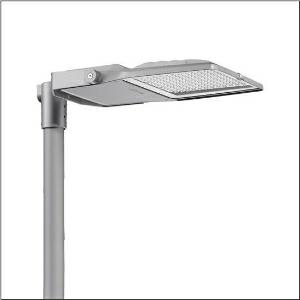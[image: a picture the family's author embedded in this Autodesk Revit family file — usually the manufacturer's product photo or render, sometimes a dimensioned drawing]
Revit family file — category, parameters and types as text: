
# Revit family: floodlight_fl_21_iq_midi___pl33t_5xa7782e4f3a_344b
name_source: partatom
category: Lighting Fixtures
units: mm (PartAtom-declared; Revit-internal decimal feet)

## family parameters
Cut with Voids When Loaded = No
Host = Face
Light Source = No
Part Type = Normal
Room Calculation Point = No
Round Connector Dimension = Use Diameter
Shared = No

## types (1)
- --- (1 x LED, 27690 lm, 208.1 W, 4000K)
    Apparent Load = 208 VA
    CIE Flux Codes = 26 75 99 100 100
    Color Rendering = 70
    Color Temperature = 4000K
    Default Elevation = 1800 mm
    Description = Floodlight FL 21 iQ midi, floodlight, primary light control with lens, of PMMA, primary optical cover: protective disc, of toughened safety glass, transparent, light distribution: PL33T, light emission: direct distribution, installation type: surface-mounted, lamps: LED, High Power LED, rated values: 27.690lm | 208,1W | 133,1lm/W (begin service life); end service life: 27.690lm | 227,1W; at 50% lumin. flux: 13.845lm | 90,3W | 153,3lm/W, colour temperature: 4000K, colour rendering: CRI > 70, light colour: 740, light setting 1 begin service life: 100% | 27.690lm | 208,1W | 133,1lm/W | 4.000K, light setting 1 end service life: 227,1W, further light settings possible, control: optimised constant luminous flux control (CLO 2.0), Desk-Remote (wireless, voltage-free reading and setting of iQ features in the workshop via application-optimized NFC function/RFID function), Smart-Wire, Night-Set, Temp-Guard, Auto-Match, Street-Remote, pre-setting: linear dimming characteristic, with terminal, 6-pole, mains connection: 220..240V, AC, 50/60Hz, luminaire housing, of diecast aluminium, powder-coated, SITECO metallic grey (DB 702S), corrosivity category C5 mid according to DIN EN ISO 12944suitable for swimming poolschlorine-resistant, sealing non-destructively replaceable, please order mast flange separately, mast bracket, of steel, galvanised, powder-coated, SITECO metallic grey (DB 702S), protection rating (complete): IP66, insulation class (complete): insulation class II (safety insulation), certification: CE, ENEC, VDE, protection symbol: D, impact resistance: IK08, permissible operating ambient temperature: -40..+40°C, permissible operating ambient temperature for outdoor applications: -40..+50°C, standard: DIN EN 12944, LABS conformity tested according to VDMA 24364:2018-05, packaging unit: 1 piece

Light Distribution: PL33T
    Height = 76 mm
    Lamp = 1 x LED
    Lamp Light Flux = 27690 lm
    Lamp Power = 208.1 W
    Lamp count = 1
    Length = 657 mm
    Luminous efficacy = 133 lm/W
    Manufacturer = Siteco
    ModVariant = No
    Model = 5XA7782E4F3A
    Number of Poles = 1
    OnlyDefault = Yes
    Power Factor = 1
    Product Name = Floodlight FL 21 iQ midi | PL33T
    Product group = floodlight | pylon annexe
    ProductGroupID = 6201
    Protection Class = Protection class II
    Protection Degree = IP 66
    RLX_Detail_Level = 1
    RLX_Emergency_Light_Flux = 0 lm
    RLX_Emergency_Type = 0
    RLX_Emergency_Type_DB = No
    RlxData = <blob elided: 153697 chars, md5=6152fdd5>
    Socket = socket
    Standby Power = 0 W
    System Light Flux = 27690 lm
    System Power = 208 W
    Type Comments = factory setting: luminous flux: 100 % | dim-lin: 254 | 710 mA
    Type Image = l_1007123.jpg
    URL = http://relux.com
    VarID = @adj_103661
    Voltage = 0 V
    Weight = 0.00 kg
    Width = 442 mm

## geometry (parser evidence)
native form markers: Blend x4, Sweep x14
no freeform markers — native parametric forms only
